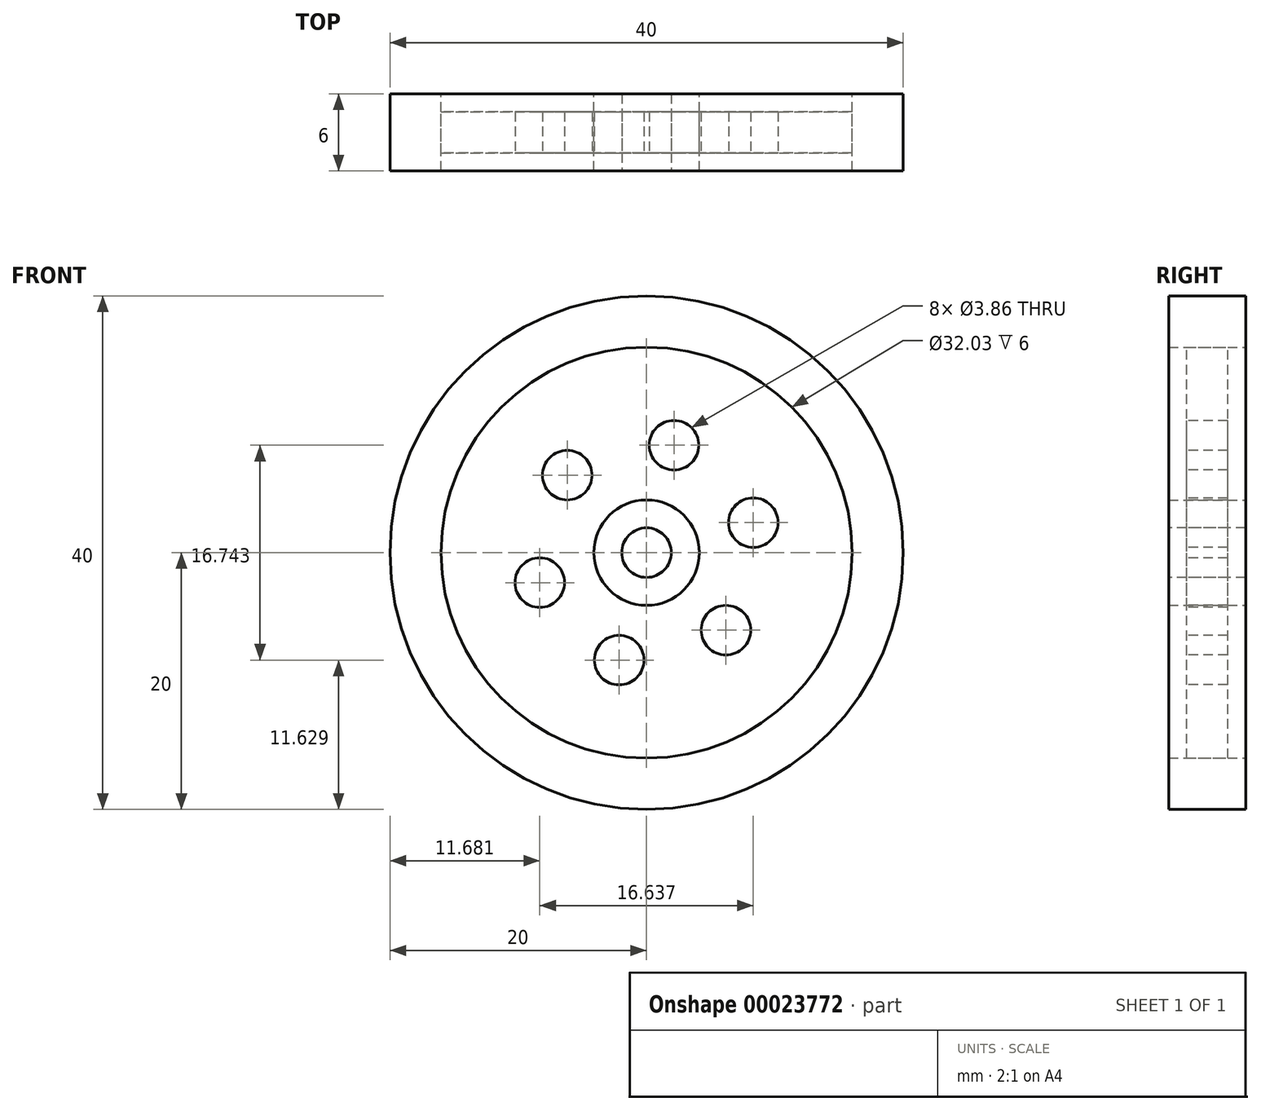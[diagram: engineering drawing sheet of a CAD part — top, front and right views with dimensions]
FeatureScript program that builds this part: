
annotation { "Feature Type Name" : "Feature", "Feature Type Description" : "" }
export const myFeature = defineFeature(function(context is Context, id is Id, definition is map)
    precondition{}
    {
        {
            var Q0;
            Q0=qCreatedBy(makeId("Front.planeOp"),FACE);
            var sketch = newSketch(context, id + "F0", { "sketchPlane" : qUnion([Q0])});
            skCircle(sketch, "E0", {"center": v(0, 0) * mm, "radius": 16.02 * mm});
            skCircle(sketch, "E1", {"center": v(0, 0) * mm, "radius": 20 * mm});
            skCircle(sketch, "E2", {"center": v(0, 0) * mm, "radius": 4.11 * mm});
            skSolve(sketch);
        }
        {
            var Q0;
            Q0 = qSketchRegion(id + "F0", true);
            var Q1;
            Q1=makeQuery(id+"F0.imprint","IMPRINT",FACE,{"disambiguationData":[TD([[makeQuery(id+"F0.imprint","IMPRINT",EDGE,{"derivedFrom":sQuery(id+"F0.wireOp",EDGE,"E2")}),1.0]])]});
            extrude(context, id + "F1", {"entities" : qUnion([Q0, Q1]), "endBound" : BoundingType.SYMMETRIC, "depth" : 6 * mm});
        }
        {
            var Q0;
            Q0=qCreatedBy(makeId("Front.planeOp"),FACE);
            var sketch = newSketch(context, id + "F2", { "sketchPlane" : qUnion([Q0])});
            skCircle(sketch, "E3", {"center": v(0, 0) * mm, "radius": 16.02 * mm});
            skSolve(sketch);
        }
        {
            var Q0;
            Q0 = qSketchRegion(id + "F2", true);
            extrude(context, id + "F3", {"entities" : qUnion([Q0]), "endBound" : BoundingType.SYMMETRIC, "depth" : 3.2 * mm});
        }
        {
            var Q0;
            Q0=makeQuery(id+"F1.opExtrude","CAP_FACE",FACE,{"disambiguationData":[OSD([sQuery(id+"F0.wireOp",EDGE,"E2")])],"isStart":false});
            var sketch = newSketch(context, id + "F4", { "sketchPlane" : qUnion([Q0])});
            skCircle(sketch, "E4", {"center": v(0, 0) * mm, "radius": 1.93 * mm});
            skSolve(sketch);
        }
        {
            var Q0;
            Q0=makeQuery(id+"F4.imprint","IMPRINT",FACE,{"disambiguationData":[TD([[makeQuery(id+"F4.imprint","IMPRINT",EDGE,{"derivedFrom":sQuery(id+"F4.wireOp",EDGE,"E4")}),1.0]])]});
            extrude(context, id + "F5", {"entities" : qUnion([Q0]), "operationType" : NewBodyOperationType.REMOVE, "oppositeDirection" : true, "depth" : 25 * mm});
        }
        {
            var Q0;
            Q0=makeQuery(id+"F3.opExtrude","CAP_FACE",FACE,{"disambiguationData":[OSD([sQuery(id+"F2.wireOp",EDGE,"E3")])],"isStart":false});
            var sketch = newSketch(context, id + "F6", { "sketchPlane" : qUnion([Q0])});
            skLineSegment(sketch, "E5", {"start": v(0, 0) * mm, "end": v(-10.18, -2.86) * mm});
            skCircle(sketch, "E6", {"center": v(-8.32, -2.33) * mm, "radius": 1.93 * mm});
            skLineSegment(sketch, "E7", {"start": v(0, 0) * mm, "end": v(-2.62, -10.24) * mm});
            skLineSegment(sketch, "E8", {"start": v(0, 0) * mm, "end": v(7.56, -7.39) * mm});
            skLineSegment(sketch, "E9", {"start": v(0, 0) * mm, "end": v(10.18, 2.86) * mm});
            skLineSegment(sketch, "E10", {"start": v(0, 0) * mm, "end": v(2.62, 10.24) * mm});
            skLineSegment(sketch, "E11", {"start": v(0, 0) * mm, "end": v(-7.56, 7.39) * mm});
            skCircle(sketch, "E12", {"center": v(-2.14, -8.37) * mm, "radius": 1.93 * mm});
            skCircle(sketch, "E13", {"center": v(6.18, -6.04) * mm, "radius": 1.93 * mm});
            skCircle(sketch, "E14", {"center": v(8.32, 2.33) * mm, "radius": 1.93 * mm});
            skCircle(sketch, "E15", {"center": v(2.14, 8.37) * mm, "radius": 1.93 * mm});
            skCircle(sketch, "E16", {"center": v(-6.18, 6.04) * mm, "radius": 1.93 * mm});
            skSolve(sketch);
        }
        {
            var Q0;
            Q0 = qSketchRegion(id + "F6", true);
            extrude(context, id + "F7", {"entities" : qUnion([Q0]), "operationType" : NewBodyOperationType.REMOVE, "endBound" : BoundingType.THROUGH_ALL, "oppositeDirection" : true, "depth" : 25 * mm});
        }
    });
